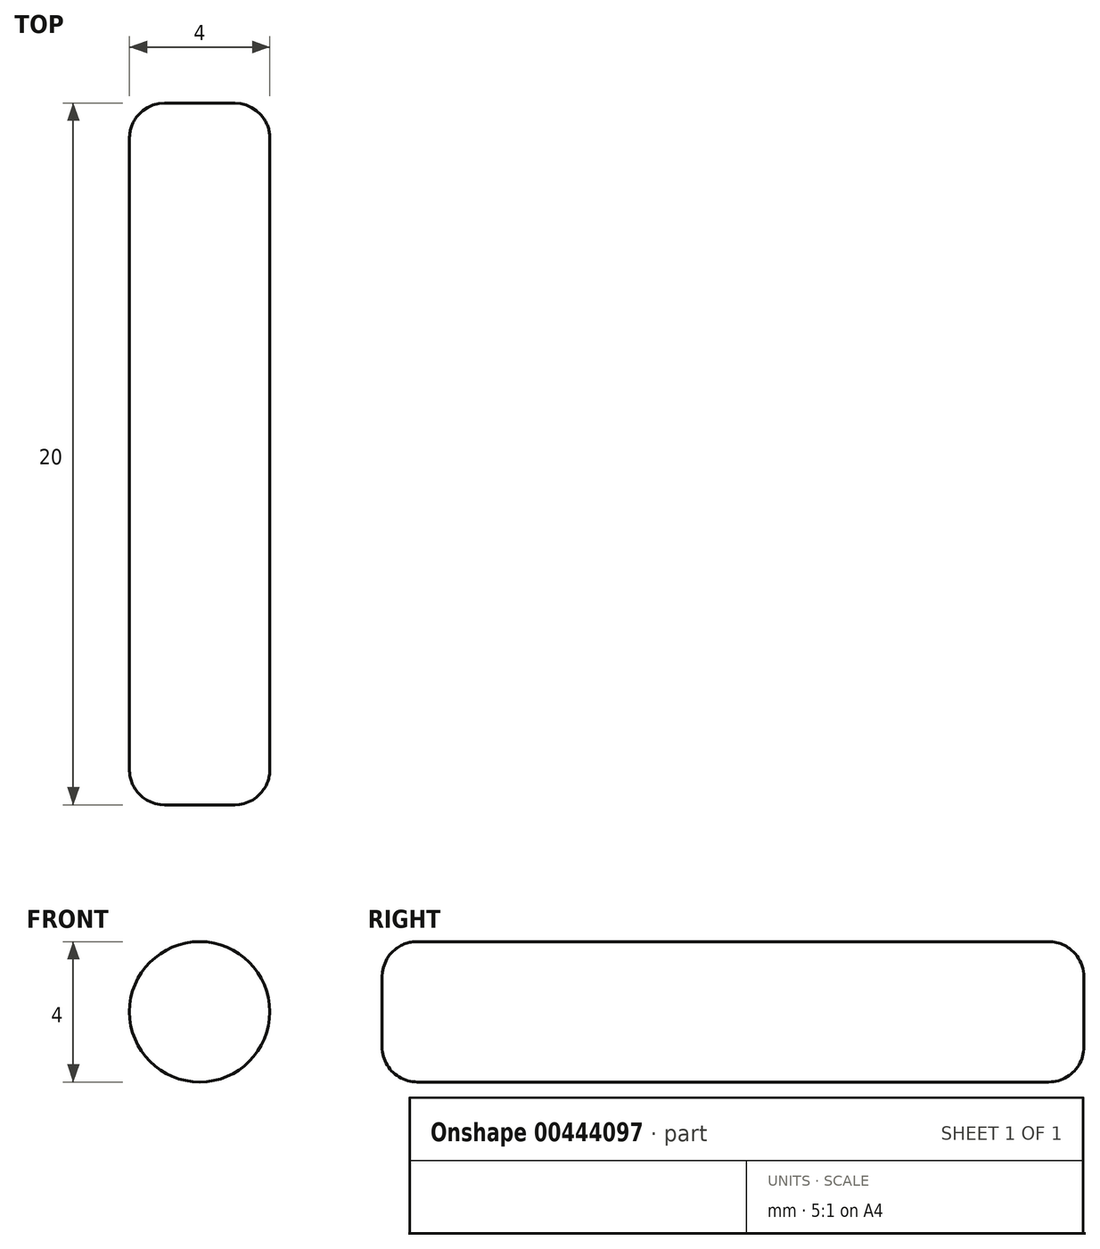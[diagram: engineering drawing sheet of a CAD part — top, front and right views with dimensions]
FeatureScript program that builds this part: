
annotation { "Feature Type Name" : "Feature", "Feature Type Description" : "" }
export const myFeature = defineFeature(function(context is Context, id is Id, definition is map)
    precondition{}
    {
        {
            var Q0;
            Q0=qCreatedBy(makeId("Front.planeOp"),FACE);
            var sketch = newSketch(context, id + "F0", { "sketchPlane" : qUnion([Q0])});
            skCircle(sketch, "E0", {"center": v(0, 0) * mm, "radius": 2 * mm});
            skSolve(sketch);
        }
        {
            var Q0;
            Q0=qSketchRegion(id+"F0",true);
            extrude(context, id + "F1", {"entities" : qUnion([Q0]), "endBound" : BoundingType.SYMMETRIC, "depth" : 20 * mm});
        }
        {
            var Q0;
            Q0=makeQuery(id+"F1.opExtrude","CAP_EDGE",EDGE,{"disambiguationData":[OSD([sQuery(id+"F0.wireOp",EDGE,"E0")])],"isStart":true});
            var Q1;
            Q1=makeQuery(id+"F1.opExtrude","CAP_EDGE",EDGE,{"disambiguationData":[OSD([sQuery(id+"F0.wireOp",EDGE,"E0")])],"isStart":false});
            fillet(context, id + "F2", {"entities" : qUnion([Q0, Q1]), "radius" : 1 * mm, "tangentPropagation" : true, "allowEdgeOverflow" : false});
        }
    });
